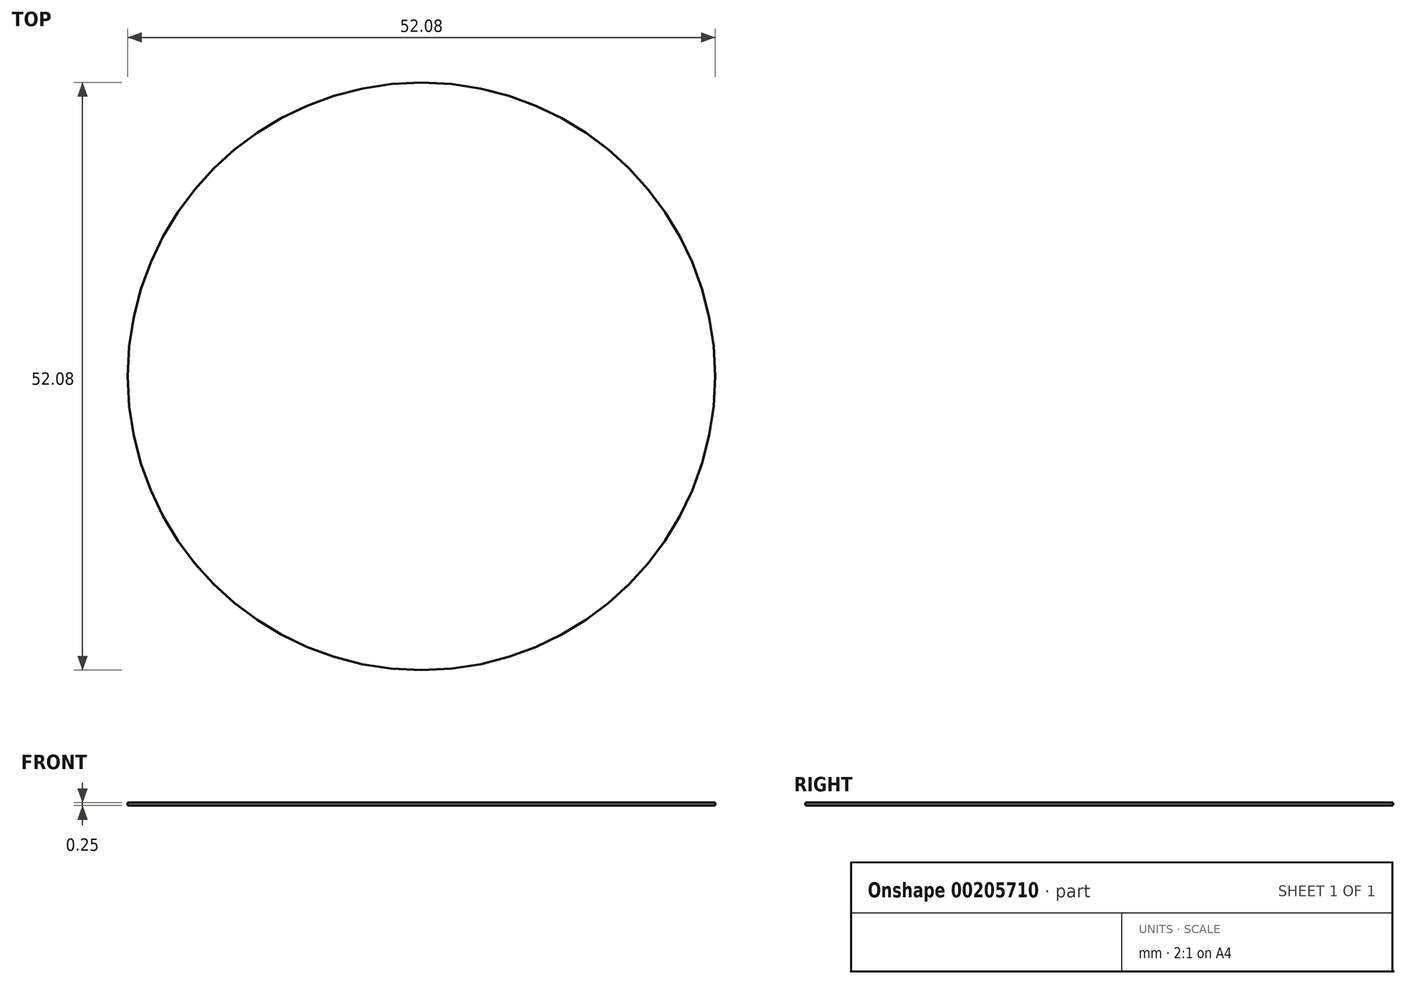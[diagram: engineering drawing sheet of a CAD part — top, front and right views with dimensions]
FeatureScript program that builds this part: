
annotation { "Feature Type Name" : "Feature", "Feature Type Description" : "" }
export const myFeature = defineFeature(function(context is Context, id is Id, definition is map)
    precondition{}
    {
        {
            var Q0;
            Q0=qCreatedBy(makeId("Top.planeOp"),FACE);
            var sketch = newSketch(context, id + "F0", { "sketchPlane" : qUnion([Q0])});
            skCircle(sketch, "E0", {"center": v(0, 0) * mm, "radius": 26.04 * mm});
            skSolve(sketch);
        }
        {
            var Q0;
            Q0 = qSketchRegion(id + "F0", true);
            extrude(context, id + "F1", {"entities" : qUnion([Q0]), "depth" : 0.25 * mm});
        }
    });
